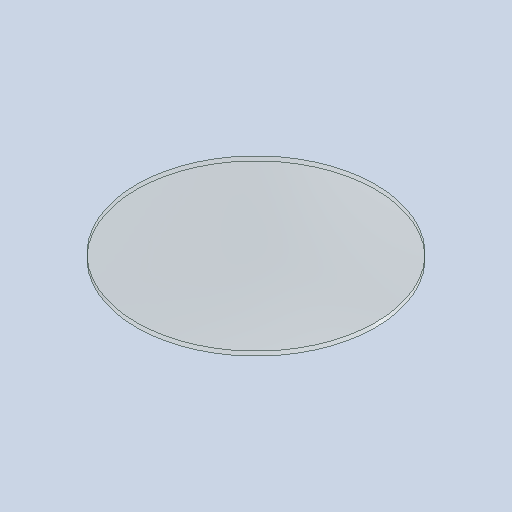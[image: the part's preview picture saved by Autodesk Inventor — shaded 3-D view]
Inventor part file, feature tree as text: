
AUTODESK INVENTOR PART (.ipt)
format: ipt  version: 2025.1 (Build 291241000, 241)  size: 237,056 bytes
history: native  units: mm
features: extrude x1, sketch x1
ambient origin geometry x8: Origin, YZ Plane, XZ Plane, XY Plane, X Axis, Y Axis, Z Axis, Center Point
bodies: Solid1 (feature_tree)
feature tree (2):
  extrude  "Extrusion1"  Depth=10.0mm TaperAngle=0.0deg
  sketch  "Sketch1"  dims[d0=550.0mm d1=10.0mm d2=0.0mm]
